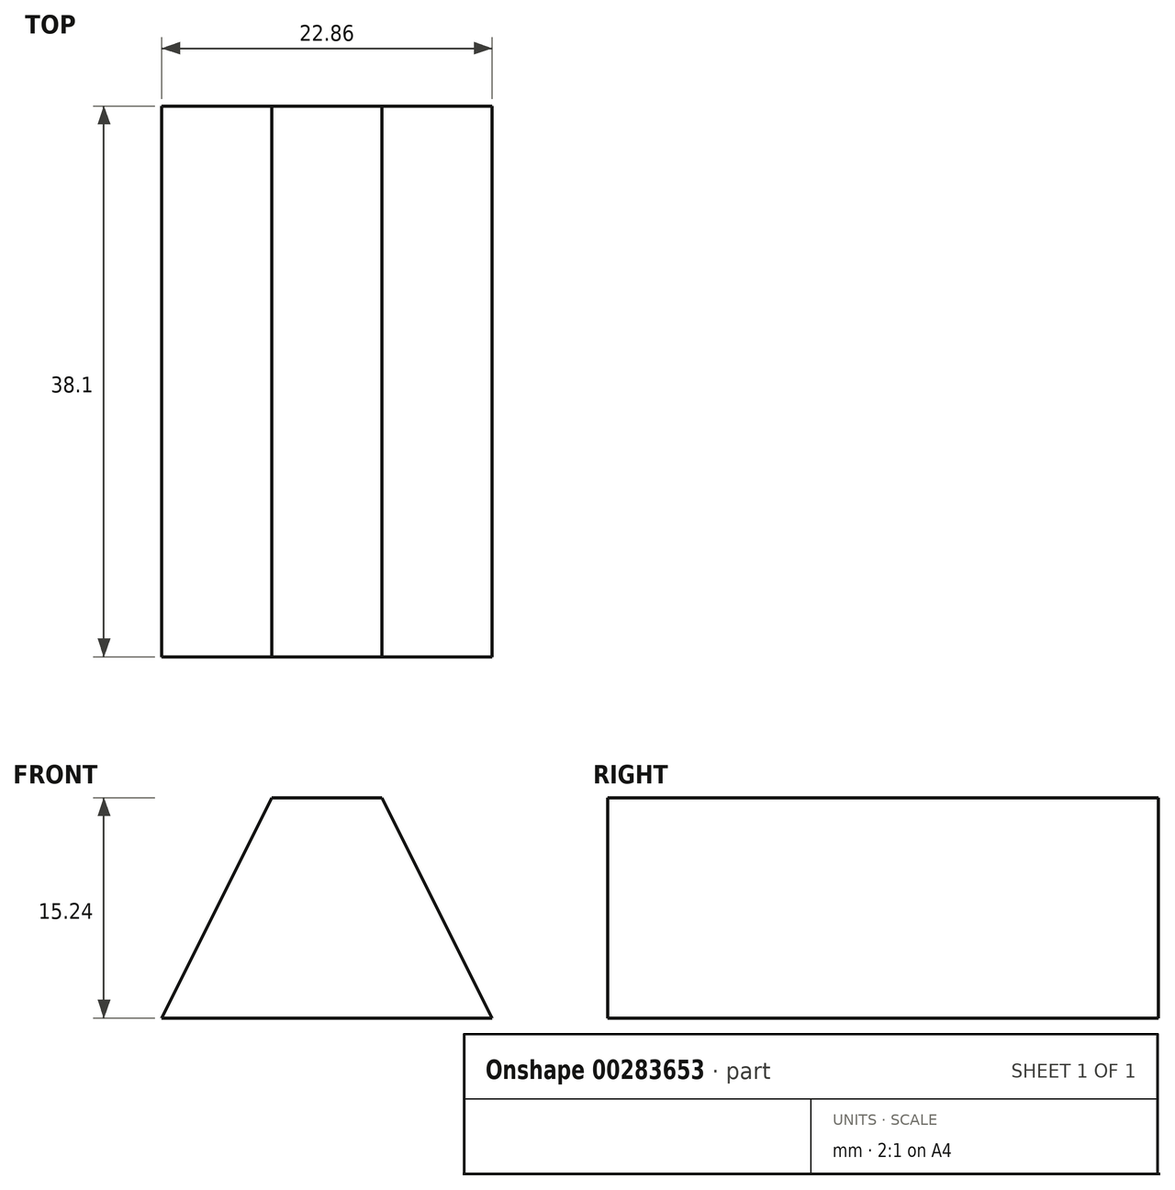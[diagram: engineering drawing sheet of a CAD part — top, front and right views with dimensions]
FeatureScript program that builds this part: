
annotation { "Feature Type Name" : "Feature", "Feature Type Description" : "" }
export const myFeature = defineFeature(function(context is Context, id is Id, definition is map)
    precondition{}
    {
        {
            var Q0;
            Q0=qCreatedBy(makeId("Front.planeOp"),FACE);
            var sketch = newSketch(context, id + "F0", { "sketchPlane" : qUnion([Q0])});
            skLineSegment(sketch, "E0", {"start": v(0, 38.1) * mm, "end": v(38.1, 38.1) * mm});
            skLineSegment(sketch, "E1", {"start": v(38.1, 38.1) * mm, "end": v(38.1, 0) * mm});
            skLineSegment(sketch, "E2", {"start": v(38.1, 0) * mm, "end": v(0, 0) * mm});
            skLineSegment(sketch, "E3", {"start": v(0, 0) * mm, "end": v(0, 38.1) * mm});
            skSolve(sketch);
        }
        {
            var Q0;
            Q0 = qSketchRegion(id + "F0", true);
            extrude(context, id + "F1", {"entities" : qUnion([Q0]), "depth" : 38.1 * mm});
        }
        {
            var Q0;
            Q0=qCreatedBy(makeId("Front.planeOp"),FACE);
            cPlane(context, id + "F2", {"entities" : qUnion([Q0]), "cplaneType" : CPlaneType.OFFSET, "offset" : 38.1 * mm, "width" : 152.4 * mm, "height" : 152.4 * mm});
        }
        {
            var Q0;
            Q0=qCreatedBy(makeId("Right.planeOp"),FACE);
            cPlane(context, id + "F3", {"entities" : qUnion([Q0]), "cplaneType" : CPlaneType.OFFSET, "offset" : 38.1 * mm, "width" : 152.4 * mm, "height" : 152.4 * mm});
        }
        {
            var Q0;
            Q0=qCreatedBy(id+"F2.planeOp",FACE);
            var sketch = newSketch(context, id + "F4", { "sketchPlane" : qUnion([Q0])});
            skLineSegment(sketch, "E4", {"start": v(0, 38.1) * mm, "end": v(38.1, 38.1) * mm});
            skLineSegment(sketch, "E5", {"start": v(38.1, 38.1) * mm, "end": v(38.1, 0) * mm});
            skLineSegment(sketch, "E6", {"start": v(38.1, 0) * mm, "end": v(0, 0) * mm});
            skLineSegment(sketch, "E7", {"start": v(0, 0) * mm, "end": v(0, 38.1) * mm});
            skLineSegment(sketch, "E8", {"start": v(0, 0) * mm, "end": v(19.05, 38.1) * mm});
            skLineSegment(sketch, "E9", {"start": v(19.05, 38.1) * mm, "end": v(38.1, 0) * mm});
            skLineSegment(sketch, "E10", {"start": v(0, 0) * mm, "end": v(7.62, 0) * mm});
            skLineSegment(sketch, "E11", {"start": v(7.62, 0) * mm, "end": v(15.24, 15.24) * mm});
            skLineSegment(sketch, "E12", {"start": v(15.24, 15.24) * mm, "end": v(22.86, 15.24) * mm});
            skLineSegment(sketch, "E13", {"start": v(22.86, 15.24) * mm, "end": v(30.48, 0) * mm});
            skLineSegment(sketch, "E14", {"start": v(30.48, 0) * mm, "end": v(38.1, 0) * mm});
            skLineSegment(sketch, "E15", {"start": v(19.95, 27.48) * mm, "end": v(17.07, 21.72) * mm});
            skLineSegment(sketch, "E16", {"start": v(17.07, 21.72) * mm, "end": v(22.6, 21.72) * mm});
            skLineSegment(sketch, "E17", {"start": v(22.6, 21.72) * mm, "end": v(19.95, 27.48) * mm});
            skSolve(sketch);
        }
        {
            var Q0;
            {var subQ0=sQuery(id+"F4.wireOp",EDGE,"E7");Q0=makeQuery(id+"F4.imprint","IMPRINT",FACE,{"disambiguationData":[TD([[makeQuery(id+"F4.imprint","IMPRINT",EDGE,{"derivedFrom":subQ0}),-1.0]])]});}
            var Q1;
            Q1=makeQuery(id+"F4.imprint","IMPRINT",FACE,{"disambiguationData":[TD([[makeQuery(id+"F4.imprint","IMPRINT",EDGE,{"derivedFrom":sQuery(id+"F4.wireOp",EDGE,"E15")}),1.0]])]});
            var Q2;
            Q2=makeQuery(id+"F4.imprint","IMPRINT",FACE,{"disambiguationData":[TD([[makeQuery(id+"F4.imprint","IMPRINT",EDGE,{"derivedFrom":sQuery(id+"F4.wireOp",EDGE,"E6")}),-1.0]])]});
            var Q3;
            {var subQ0=sQuery(id+"F4.wireOp",EDGE,"E5");Q3=makeQuery(id+"F4.imprint","IMPRINT",FACE,{"disambiguationData":[TD([[makeQuery(id+"F4.imprint","IMPRINT",EDGE,{"derivedFrom":subQ0}),-1.0]])]});}
            extrude(context, id + "F5", {"entities" : qUnion([Q0, Q1, Q2, Q3]), "operationType" : NewBodyOperationType.REMOVE, "oppositeDirection" : true, "depth" : 38.1 * mm});
        }
        {
            var Q0;
            Q0=qCreatedBy(id+"F3.planeOp",FACE);
            var sketch = newSketch(context, id + "F6", { "sketchPlane" : qUnion([Q0])});
            skCircle(sketch, "E18", {"center": v(-33.02, 33.47) * mm, "radius": 1.59 * mm});
            skSolve(sketch);
        }
        {
            var Q0;
            Q0=makeQuery(id+"F6.imprint","IMPRINT",FACE,{"disambiguationData":[TD([[makeQuery(id+"F6.imprint","IMPRINT",EDGE,{"derivedFrom":sQuery(id+"F6.wireOp",EDGE,"E18")}),1.0]])]});
            extrude(context, id + "F7", {"entities" : qUnion([Q0]), "operationType" : NewBodyOperationType.REMOVE, "oppositeDirection" : true, "depth" : 38.1 * mm});
        }
    });
